# Revit family: 2-5-16_Sliding-Door_TX9200SL_Bipart-Outside-Slide-w-Transom-O-SX-SX-O-w-Elec-Lock-Flush-Mnt-Exit-Panic-HW_Tormax
name_source: partatom
category: Doors
units: mm (PartAtom-declared; Revit-internal decimal feet)

## family parameters
Always vertical = Yes
Classification Number = 23.30.10.00
Cut with Voids When Loaded = No
Host = Wall
Room Calculation Point = No
Shared = No

## types (3) — shared parameters
Analytic Construction = <None>
CAD Details = https://www.arcat.com
Define Thermal Properties by = Schematic Type
Door Height = 11' - 0"
Frame Material = Aluminum - Tormax
Frame Projection Ext. = 0' - 0"
Frame Projection Int. = 0' - 0"
Frame Width = 0' - 0"
Glass = Glass - Tormax
Height = 11' - 0"
Keynote = 08 42 29
Manufacturer = Tormax
Model = TX9200SL
Product Page URL = https://www.arcat.com
Rough Height = 11' - 0 1/4"
Specification = https://www.arcat.com
Thickness = 0' - 4 1/2"
URL = https://www.tormaxusa.com
Wall Closure = By host

## per-type parameters (varying)
| type | Description | Door Width | Rough Width | Width |
| 10'-0" Package Width | Bipart Outside Slide Application w/ Transom (O-SX-SX-O) w/ Electric Lock & Flush Mount Exit Panic HDW, 10'-0" Package Width | 2' - 6 7/16" | 10' - 0 1/2" | 10' - 0" |
| 12'-0" Package Width | Bipart Outside Slide Application w/ Transom (O-SX-SX-O) w/ Electric Lock & Flush Mount Exit Panic HDW, 12'-0" Package Width | 3' - 0 7/16" | 12' - 0 1/2" | 12' - 0" |
| 14'-0" Package Width | Bipart Outside Slide Application w/ Transom (O-SX-SX-O) w/ Electric Lock & Flush Mount Exit Panic HDW, 14'-0" Package Width | 3' - 6 7/16" | 14' - 0 1/2" | 14' - 0" |

## geometry (parser evidence)
native form markers: Sweep x8
no freeform markers — native parametric forms only
